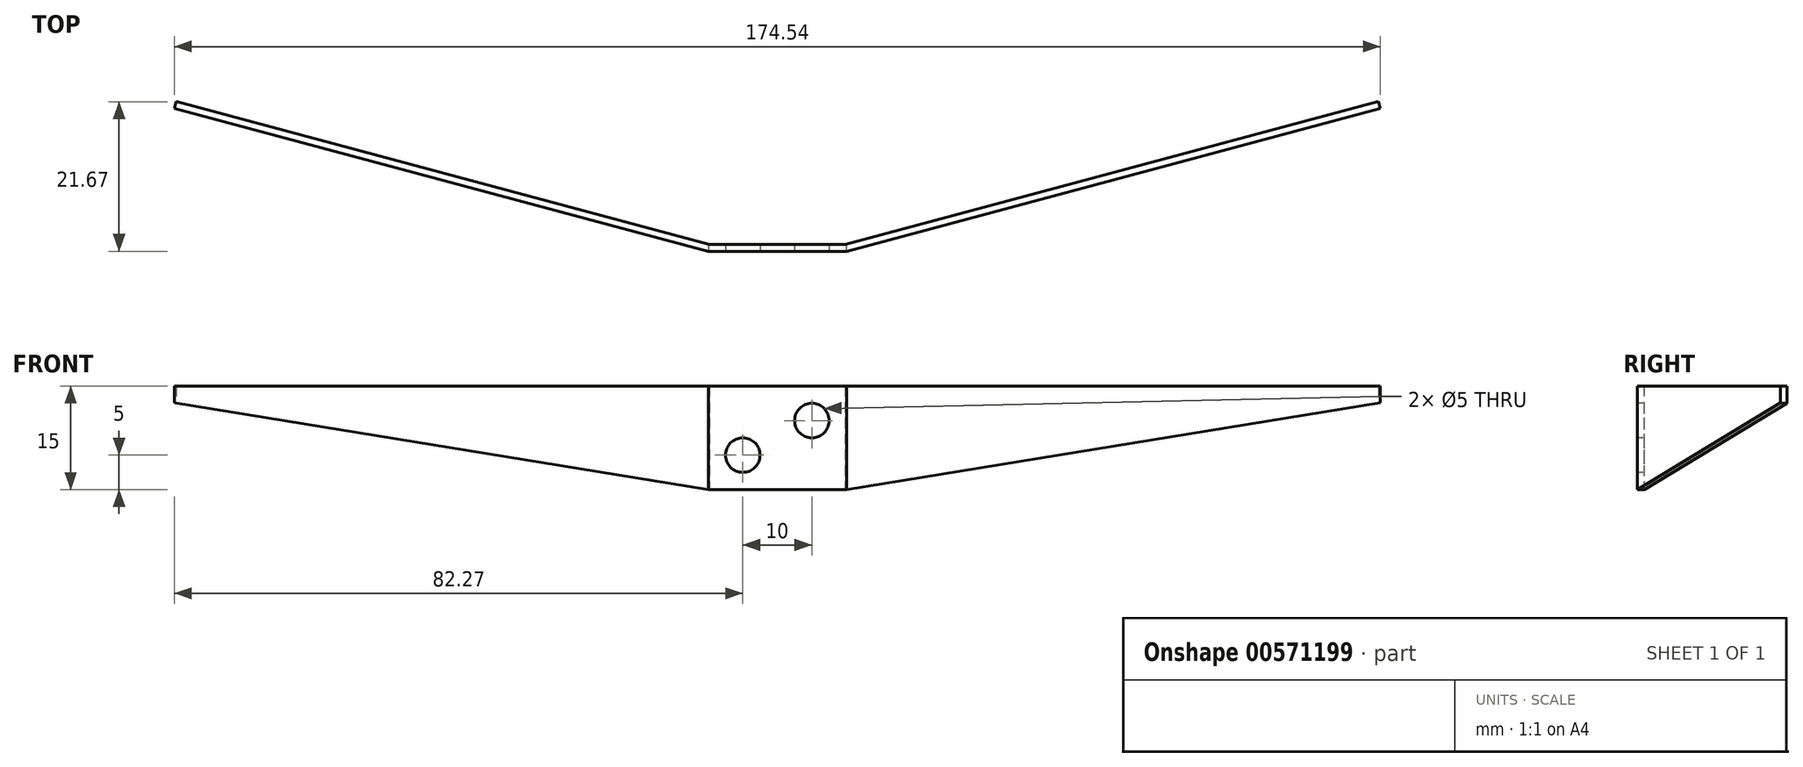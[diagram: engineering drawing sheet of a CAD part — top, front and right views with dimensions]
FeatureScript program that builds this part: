
annotation { "Feature Type Name" : "Feature", "Feature Type Description" : "" }
export const myFeature = defineFeature(function(context is Context, id is Id, definition is map)
    precondition{}
    {
        {
            var Q0;
            Q0=qCreatedBy(makeId("Top.planeOp"),FACE);
            var sketch = newSketch(context, id + "F0", { "sketchPlane" : qUnion([Q0])});
            skLineSegment(sketch, "E0", {"start": v(0, 0) * mm, "end": v(-77.27, 20.7) * mm});
            skLineSegment(sketch, "E1", {"start": v(-77.27, 20.7) * mm, "end": v(-77.02, 21.67) * mm});
            skLineSegment(sketch, "E2", {"start": v(-77.02, 21.67) * mm, "end": v(0.13, 1) * mm});
            skLineSegment(sketch, "E3", {"start": v(0.13, 1) * mm, "end": v(19.87, 1) * mm});
            skLineSegment(sketch, "E4", {"start": v(0, 0) * mm, "end": v(20, 0) * mm});
            skLineSegment(sketch, "E5", {"start": v(19.87, 1) * mm, "end": v(97.02, 21.67) * mm});
            skLineSegment(sketch, "E6", {"start": v(20, 0) * mm, "end": v(97.27, 20.7) * mm});
            skLineSegment(sketch, "E7", {"start": v(97.02, 21.67) * mm, "end": v(97.27, 20.7) * mm});
            skSolve(sketch);
        }
        {
            var Q0;
            Q0=makeQuery(id+"F0.imprint","IMPRINT",FACE,{"disambiguationData":[TD([[makeQuery(id+"F0.imprint","IMPRINT",EDGE,{"derivedFrom":sQuery(id+"F0.wireOp",EDGE,"E0")}),-1.0]])]});
            extrude(context, id + "F1", {"entities" : qUnion([Q0]), "depth" : 15 * mm, "offsetDistance" : 25 * mm});
        }
        {
            var Q0;
            Q0=qCreatedBy(makeId("Front.planeOp"),FACE);
            var sketch = newSketch(context, id + "F2", { "sketchPlane" : qUnion([Q0])});
            skLineSegment(sketch, "E8", {"start": v(0, 0) * mm, "end": v(-80, 13) * mm});
            skLineSegment(sketch, "E9", {"start": v(-80, 13) * mm, "end": v(-80, 0) * mm});
            skLineSegment(sketch, "E10", {"start": v(-80, 0) * mm, "end": v(0, 0) * mm});
            skLineSegment(sketch, "E11", {"start": v(19.98, 0) * mm, "end": v(99.98, 13) * mm});
            skLineSegment(sketch, "E12", {"start": v(99.98, 13) * mm, "end": v(99.98, 0) * mm});
            skLineSegment(sketch, "E13", {"start": v(99.98, 0) * mm, "end": v(19.98, 0) * mm});
            skSolve(sketch);
        }
        {
            var Q0;
            Q0=makeQuery(id+"F2.imprint","IMPRINT",FACE,{"disambiguationData":[TD([[makeQuery(id+"F2.imprint","IMPRINT",EDGE,{"derivedFrom":sQuery(id+"F2.wireOp",EDGE,"E8")}),1.0]])]});
            var Q1;
            Q1=makeQuery(id+"F2.imprint","IMPRINT",FACE,{"disambiguationData":[TD([[makeQuery(id+"F2.imprint","IMPRINT",EDGE,{"derivedFrom":sQuery(id+"F2.wireOp",EDGE,"E11")}),-1.0]])]});
            extrude(context, id + "F3", {"entities" : qUnion([Q0, Q1]), "operationType" : NewBodyOperationType.REMOVE, "endBound" : BoundingType.THROUGH_ALL, "oppositeDirection" : true, "depth" : 25 * mm, "offsetDistance" : 25 * mm});
        }
        {
            var Q0;
            Q0=makeQuery(id+"F1.opExtrude","SWEPT_FACE",FACE,{"disambiguationData":[OSD([sQuery(id+"F0.wireOp",EDGE,"E4")])]});
            var sketch = newSketch(context, id + "F4", { "sketchPlane" : qUnion([Q0])});
            skPoint(sketch, "E14", {"position": v(5, 5) * mm});
            skPoint(sketch, "E15", {"position": v(15, 10) * mm});
            skSolve(sketch);
        }
        {
            var Q0;
            Q0=sQuery(id+"F4.wireOp",VERTEX,"E14");
            var Q1;
            Q1=sQuery(id+"F4.wireOp",VERTEX,"E15");
            var Q2;
            Q2=makeQuery(id+"F1.opExtrude","SWEPT_BODY",BODY,{"disambiguationData":[OSD([sQuery(id+"F0.wireOp",EDGE,"E0"),sQuery(id+"F0.wireOp",EDGE,"E1"),sQuery(id+"F0.wireOp",EDGE,"E2"),sQuery(id+"F0.wireOp",EDGE,"E3"),sQuery(id+"F0.wireOp",EDGE,"E4"),sQuery(id+"F0.wireOp",EDGE,"E5"),sQuery(id+"F0.wireOp",EDGE,"E6"),sQuery(id+"F0.wireOp",EDGE,"E7")])]});
            hole(context, id + "F5", {"style" : HoleStyle.SIMPLE, "endStyle" : HoleEndStyle.THROUGH, "holeDiameter" : 5 * mm, "isTappedThrough" : true, "tappedDepth" : 12 * mm, "tapClearance" : 3, "locations" : qUnion([Q0, Q1]), "scope" : qUnion([Q2])});
        }
    });
